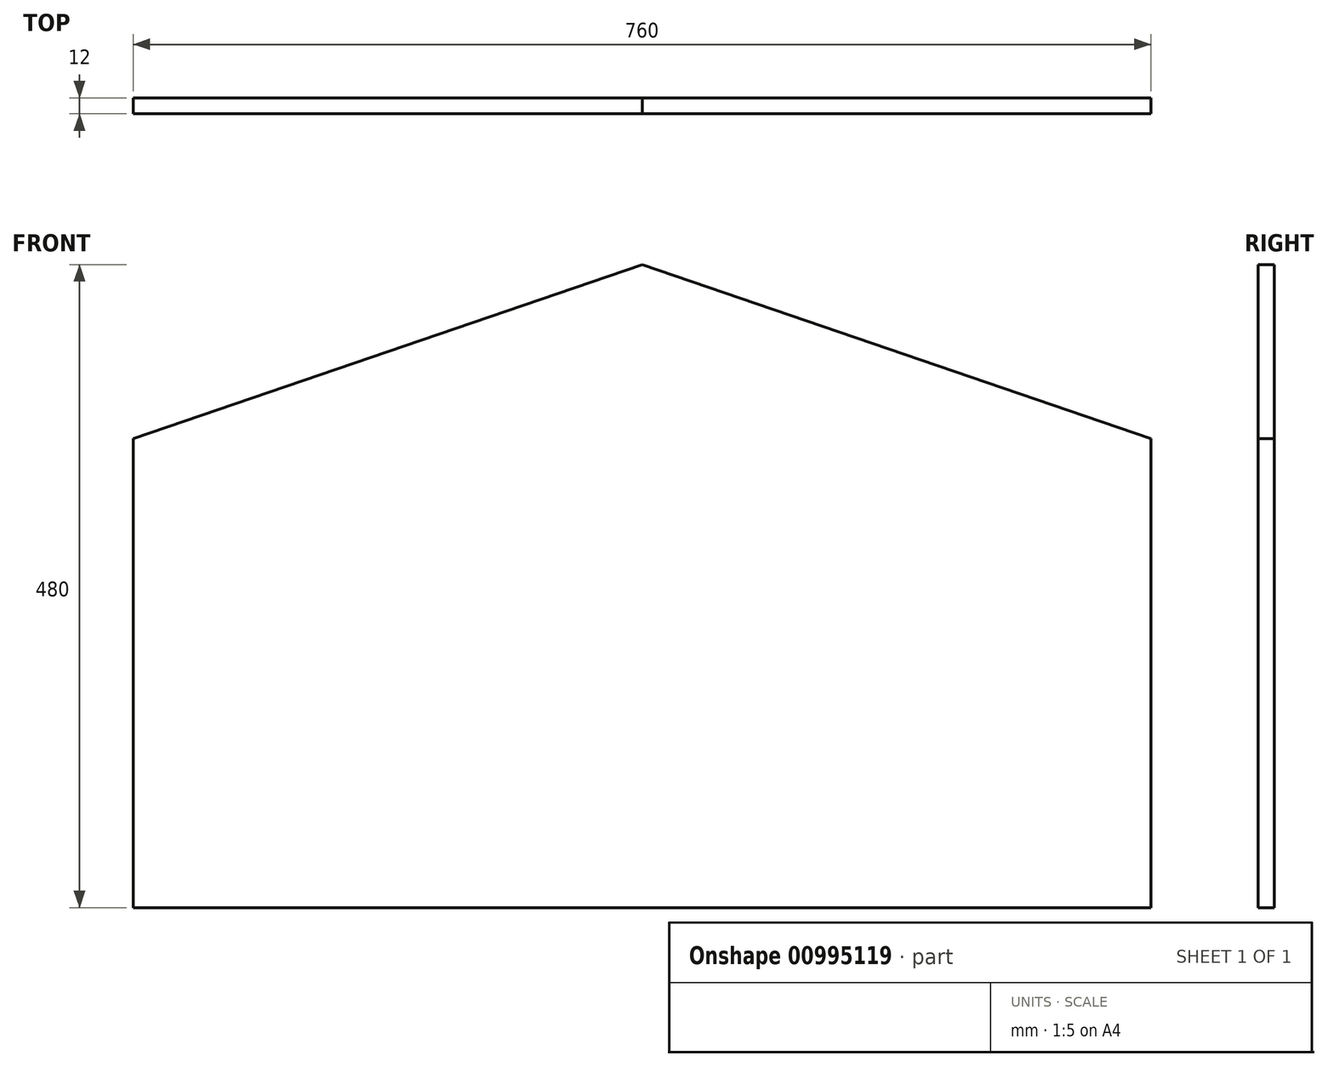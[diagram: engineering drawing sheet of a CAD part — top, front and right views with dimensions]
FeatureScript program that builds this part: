
annotation { "Feature Type Name" : "Feature", "Feature Type Description" : "" }
export const myFeature = defineFeature(function(context is Context, id is Id, definition is map)
    precondition{}
    {
        {
            var Q0;
            Q0=qCreatedBy(makeId("Front.planeOp"),FACE);
            var sketch = newSketch(context, id + "F0", { "sketchPlane" : qUnion([Q0])});
            skLineSegment(sketch, "E0", {"start": v(-380, 0) * mm, "end": v(-380, 350) * mm});
            skLineSegment(sketch, "E1", {"start": v(-380, 350) * mm, "end": v(0, 480) * mm});
            skLineSegment(sketch, "E2", {"start": v(0, 480) * mm, "end": v(380, 350) * mm});
            skLineSegment(sketch, "E3", {"start": v(380, 350) * mm, "end": v(380, 0) * mm});
            skLineSegment(sketch, "E4", {"start": v(380, 0) * mm, "end": v(-380, 0) * mm});
            skSolve(sketch);
        }
        {
            var Q0;
            Q0=qSketchRegion(id+"F0",true);
            extrude(context, id + "F1", {"entities" : qUnion([Q0]), "depth" : 12 * mm, "offsetDistance" : 25 * mm});
        }
    });
